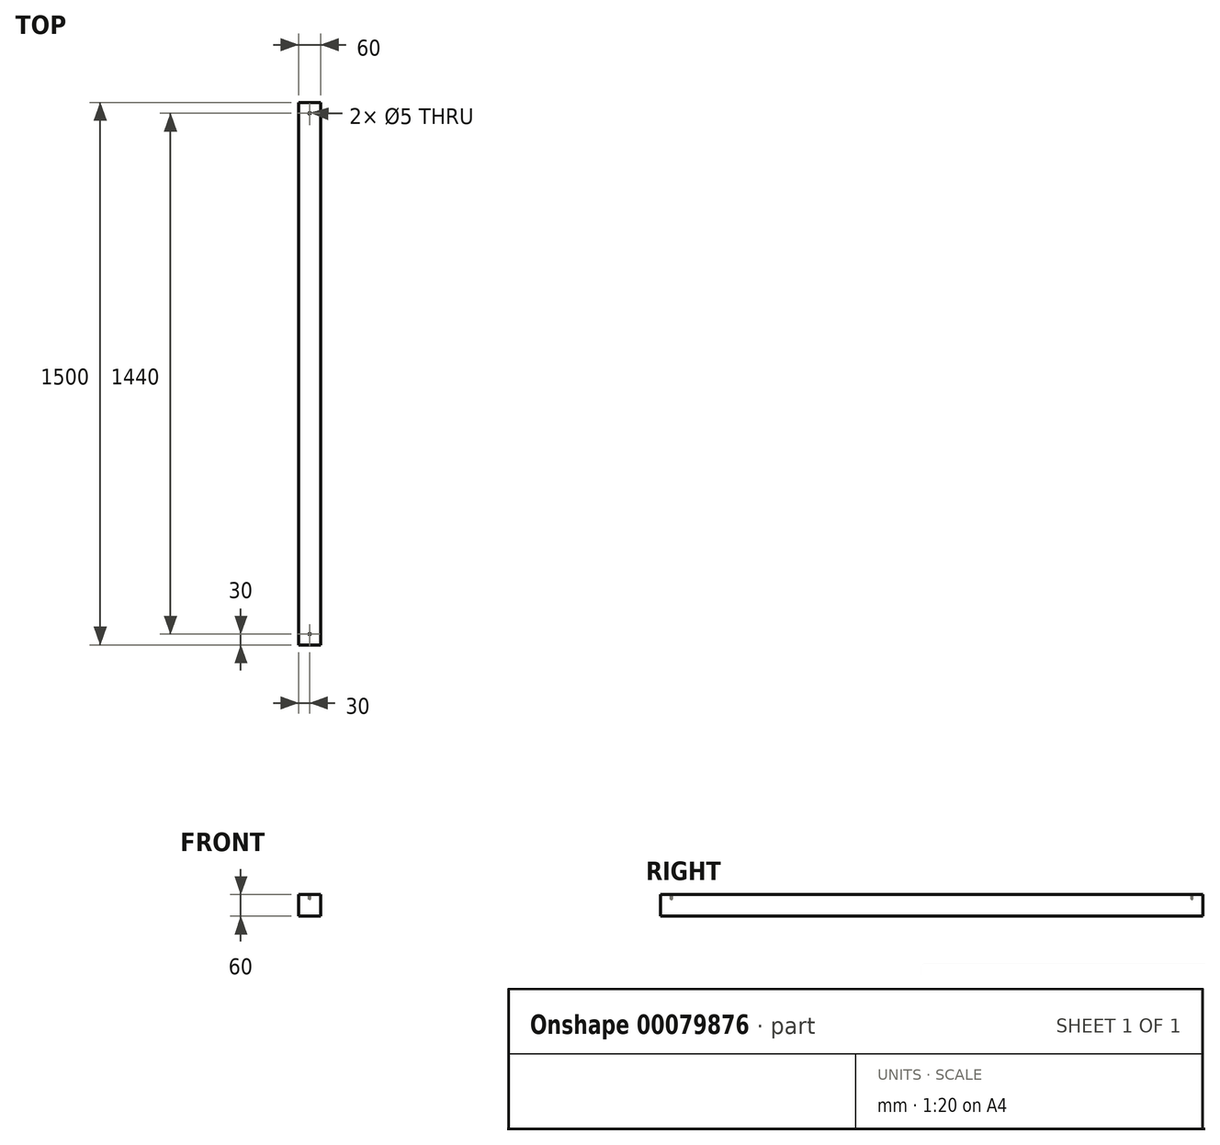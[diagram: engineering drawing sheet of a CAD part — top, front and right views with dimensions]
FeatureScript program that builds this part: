
annotation { "Feature Type Name" : "Feature", "Feature Type Description" : "" }
export const myFeature = defineFeature(function(context is Context, id is Id, definition is map)
    precondition{}
    {
        {
            assignVariable(context, id + "F0", {"name" : "bed_length", "anyValue" : 1500 * mm});
        }
        {
            assignVariable(context, id + "F1", {"name" : "hole_diameter", "anyValue" : 5});
        }
        {
            assignVariable(context, id + "F2", {"name" : "hole_length", "anyValue" : 12});
        }
        {
            var Q0;
            Q0=qCreatedBy(makeId("Front.planeOp"),FACE);
            var sketch = newSketch(context, id + "F3", { "sketchPlane" : qUnion([Q0])});
            skLineSegment(sketch, "E0.bottom", {"start": v(0, 0) * mm, "end": v(60, 0) * mm});
            skLineSegment(sketch, "E0.top", {"start": v(0, 60) * mm, "end": v(60, 60) * mm});
            skLineSegment(sketch, "E0.left", {"start": v(0, 0) * mm, "end": v(0, 60) * mm});
            skLineSegment(sketch, "E0.right", {"start": v(60, 0) * mm, "end": v(60, 60) * mm});
            skSolve(sketch);
        }
        {
            var Q0;
            Q0=makeQuery(id+"F3.imprint","IMPRINT",FACE,{"disambiguationData":[TD([[makeQuery(id+"F3.imprint","IMPRINT",EDGE,{"derivedFrom":sQuery(id+"F3.wireOp",EDGE,"E0.bottom")}),1.0]])]});
            extrude(context, id + "F4", {"entities" : qUnion([Q0]), "depth" : getVariable(context, 'bed_length')});
        }
        {
            var Q0;
            Q0=makeQuery(id+"F4.opExtrude","SWEPT_FACE",FACE,{"disambiguationData":[OSD([sQuery(id+"F3.wireOp",EDGE,"E0.top")])]});
            var sketch = newSketch(context, id + "F5", { "sketchPlane" : qUnion([Q0])});
            skPoint(sketch, "E1", {"position": v(30, -1470) * mm});
            skPoint(sketch, "E1.positionSnap0", {"position": v(30, -1500) * mm});
            skPoint(sketch, "E2", {"position": v(30, -30) * mm});
            skPoint(sketch, "E2.positionSnap0", {"position": v(30, 0) * mm});
            skSolve(sketch);
        }
        {
            var Q0;
            Q0=sQuery(id+"F5.wireOp",VERTEX,"E1");
            var Q1;
            Q1=sQuery(id+"F5.wireOp",VERTEX,"E2");
            var Q2;
            Q2=makeQuery(id+"F4.opExtrude","SWEPT_BODY",BODY,{"disambiguationData":[OSD([sQuery(id+"F3.wireOp",EDGE,"E0.bottom"),sQuery(id+"F3.wireOp",EDGE,"E0.top"),sQuery(id+"F3.wireOp",EDGE,"E0.left"),sQuery(id+"F3.wireOp",EDGE,"E0.right")])]});
            hole(context, id + "F6", {"style" : HoleStyle.SIMPLE, "endStyle" : HoleEndStyle.BLIND, "holeDiameter" : (getVariable(context, 'hole_diameter')) * mm, "holeDepth" : (getVariable(context, 'hole_length')) * mm, "locations" : qUnion([Q0, Q1]), "scope" : qUnion([Q2])});
        }
    });
